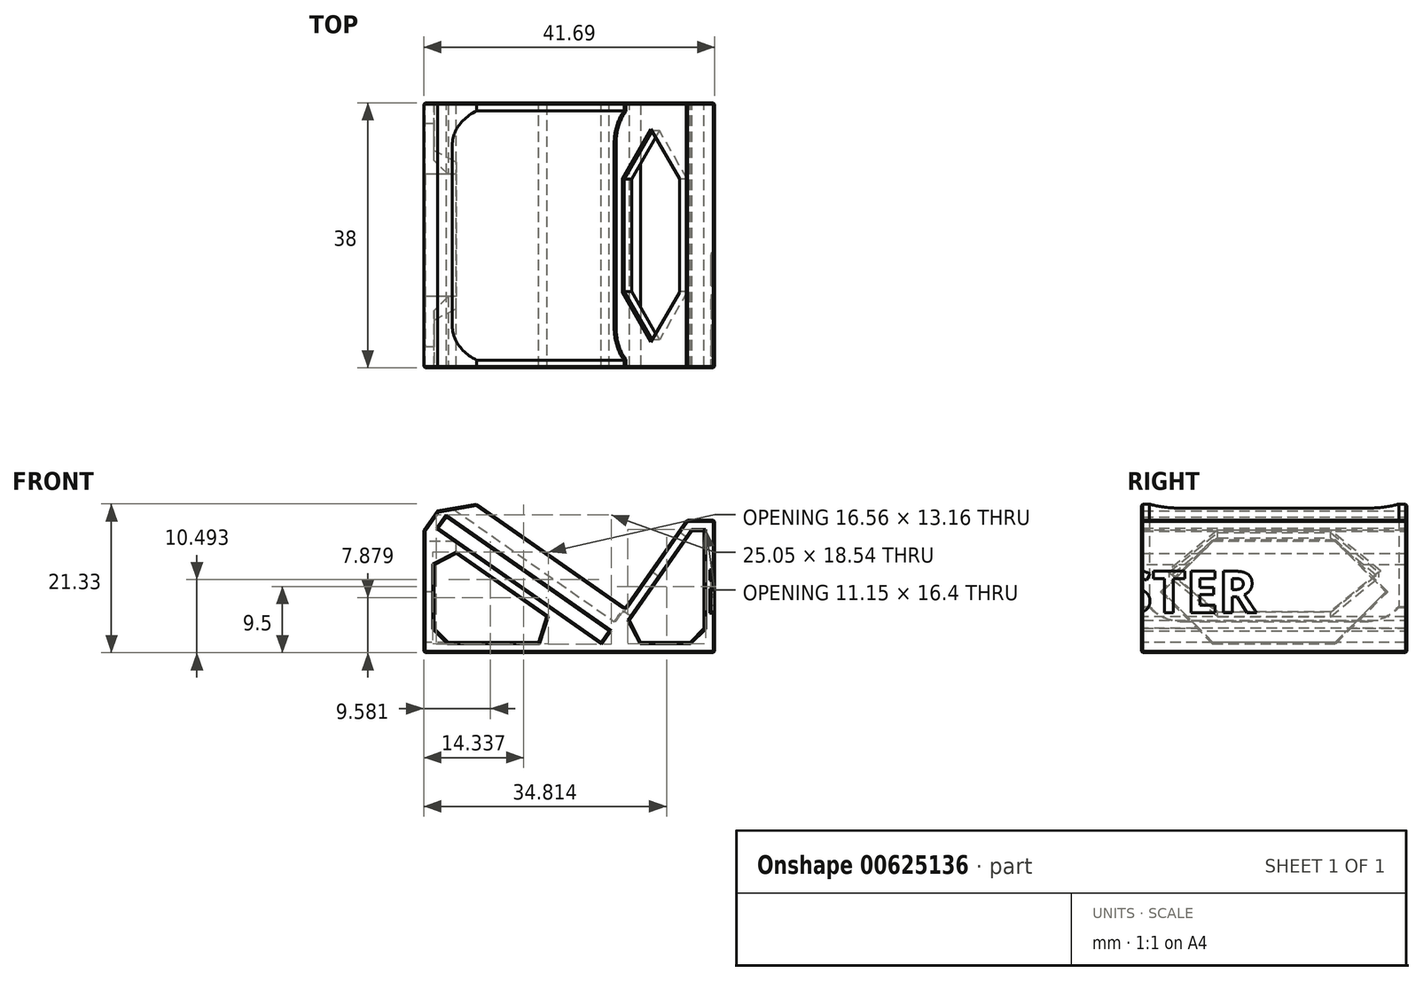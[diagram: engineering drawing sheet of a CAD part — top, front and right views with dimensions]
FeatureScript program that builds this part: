
annotation { "Feature Type Name" : "Feature", "Feature Type Description" : "" }
export const myFeature = defineFeature(function(context is Context, id is Id, definition is map)
    precondition{}
    {
        {
            var Q0;
            Q0=qCreatedBy(makeId("Front.planeOp"),FACE);
            var sketch = newSketch(context, id + "F0", { "sketchPlane" : qUnion([Q0])});
            skLineSegment(sketch, "E0", {"start": v(0, 0) * mm, "end": v(0, 19) * mm});
            skLineSegment(sketch, "E1", {"start": v(-4, 19) * mm, "end": v(-14.25, 4.37) * mm});
            skLineSegment(sketch, "E2", {"start": v(-14.25, 4.37) * mm, "end": v(-38.82, 21.57) * mm});
            skLineSegment(sketch, "E3", {"start": v(-18.87, 1.5) * mm, "end": v(-40.19, 16.43) * mm});
            skPoint(sketch, "E4", {"position": v(0, 0) * mm});
            skLineSegment(sketch, "E5", {"start": v(-38.45, 19.49) * mm, "end": v(-15.1, 3.14) * mm});
            skLineSegment(sketch, "E6", {"start": v(-15.1, 3.14) * mm, "end": v(-16.25, 1.5) * mm});
            skLineSegment(sketch, "E7", {"start": v(0, 19) * mm, "end": v(-4, 19) * mm});
            skLineSegment(sketch, "E8", {"start": v(-14.42, 1.5) * mm, "end": v(-3.22, 17.5) * mm});
            skLineSegment(sketch, "E9", {"start": v(-3.22, 17.5) * mm, "end": v(-1.5, 17.5) * mm});
            skLineSegment(sketch, "E10", {"start": v(-1.5, 17.5) * mm, "end": v(-1.5, 1.5) * mm});
            skLineSegment(sketch, "E11", {"start": v(-1.5, 1.5) * mm, "end": v(-14.42, 1.5) * mm});
            skLineSegment(sketch, "E12", {"start": v(-16.25, 1.5) * mm, "end": v(-39.6, 17.85) * mm});
            skLineSegment(sketch, "E13", {"start": v(-38.45, 19.49) * mm, "end": v(-39.6, 17.85) * mm});
            skLineSegment(sketch, "E14", {"start": v(-38.82, 21.57) * mm, "end": v(-41.69, 17.48) * mm});
            skLineSegment(sketch, "E15", {"start": v(-41.69, 17.48) * mm, "end": v(-41.69, 0) * mm});
            skLineSegment(sketch, "E16", {"start": v(-41.69, 0) * mm, "end": v(0, 0) * mm});
            skLineSegment(sketch, "E17.0", {"start": v(-40.19, 1.5) * mm, "end": v(-18.87, 1.5) * mm});
            skLineSegment(sketch, "E17.1", {"start": v(-40.19, 16.43) * mm, "end": v(-40.19, 1.5) * mm});
            skSolve(sketch);
        }
        {
            var Q0;
            {var subQ3=sQuery(id+"F0.wireOp",EDGE,"E2");Q0=makeQuery(id+"F0.imprint","IMPRINT",FACE,{"disambiguationData":[TD([[makeQuery(id+"F0.imprint","IMPRINT",EDGE,{"derivedFrom":subQ3}),1.0]])]});}
            extrude(context, id + "F1", {"entities" : qUnion([Q0]), "endBound" : BoundingType.SYMMETRIC, "depth" : 38 * mm, "offsetDistance" : 25 * mm});
        }
        {
            var Q0;
            Q0=makeQuery(id+"F1.opExtrude","SWEPT_FACE",FACE,{"disambiguationData":[OSD([sQuery(id+"F0.wireOp",EDGE,"E0")])]});
            var sketch = newSketch(context, id + "F2", { "sketchPlane" : qUnion([Q0])});
            skText(sketch, "E18", { "text": "AIRSTER", "fontName": "OpenSans-Bold.ttf"});
            skPoint(sketch, "E19", {"position": v(-17, 9.5) * mm});
            skPoint(sketch, "E20", {"position": v(-19, 9.5) * mm});
            skPoint(sketch, "E21", {"position": v(0, 19) * mm});
            const initialGuessF2  = {"E18": [-0.036, 0.00576, 1, 0, 0.00598]};
            skSetInitialGuess(sketch, initialGuessF2);
            skSolve(sketch);
        }
        {
            var Q0;
            Q0=qSketchRegion(id+"F2",true);
            extrude(context, id + "F3", {"entities" : qUnion([Q0]), "operationType" : NewBodyOperationType.REMOVE, "oppositeDirection" : true, "depth" : 0.5 * mm});
        }
        {
            var Q0;
            Q0=makeQuery(id+"F1.opExtrude","SWEPT_EDGE",EDGE,{"disambiguationData":[OSD([sQuery(id+"F0.wireOp",EDGE,"E8"),sQuery(id+"F0.wireOp",EDGE,"E11")])]});
            var Q1;
            Q1=makeQuery(id+"F1.opExtrude","SWEPT_EDGE",EDGE,{"disambiguationData":[OSD([sQuery(id+"F0.wireOp",EDGE,"E10"),sQuery(id+"F0.wireOp",EDGE,"E11")])]});
            var Q2;
            Q2=makeQuery(id+"F1.opExtrude","SWEPT_EDGE",EDGE,{"disambiguationData":[OSD([sQuery(id+"F0.wireOp",EDGE,"E17.0"),sQuery(id+"F0.wireOp",EDGE,"E17.1")])]});
            var Q3;
            Q3=makeQuery(id+"F1.opExtrude","SWEPT_EDGE",EDGE,{"disambiguationData":[OSD([sQuery(id+"F0.wireOp",EDGE,"E3"),sQuery(id+"F0.wireOp",EDGE,"E17.1")])]});
            chamfer(context, id + "F4", {"entities" : qUnion([Q0, Q1, Q2, Q3]), "width" : 2 * mm, "tangentPropagation" : true});
        }
        {
            var Q0;
            Q0=makeQuery(id+"F1.opExtrude","SWEPT_FACE",FACE,{"disambiguationData":[OSD([sQuery(id+"F0.wireOp",EDGE,"E1")])]});
            var sketch = newSketch(context, id + "F5", { "sketchPlane" : qUnion([Q0])});
            skArc(sketch, "E22", {"start": v(-19, 1.4) * mm, "mid": v(-17.24, -2.84) * mm, "end": v(-13, -4.6) * mm});
            skArc(sketch, "E23.MirrorCS", {"start": v(19, 1.4) * mm, "mid": v(17.24, -2.84) * mm, "end": v(13, -4.6) * mm});
            skLineSegment(sketch, "E24", {"start": v(-19, -2.1) * mm, "end": v(-17.87, -2.1) * mm});
            skLineSegment(sketch, "E25.MirrorCS", {"start": v(19, -2.1) * mm, "end": v(17.87, -2.1) * mm});
            skLineSegment(sketch, "E26", {"start": v(0, 11.27) * mm, "end": v(-15, 11.27) * mm});
            skLineSegment(sketch, "E27", {"start": v(-15, 11.27) * mm, "end": v(-15, -2.6) * mm});
            skLineSegment(sketch, "E28", {"start": v(-15, -2.6) * mm, "end": v(0, -2.6) * mm});
            skLineSegment(sketch, "E29.MirrorCS", {"start": v(0, 11.27) * mm, "end": v(15, 11.27) * mm});
            skLineSegment(sketch, "E30.MirrorCS", {"start": v(15, 11.27) * mm, "end": v(15, -2.6) * mm});
            skLineSegment(sketch, "E31.MirrorCS", {"start": v(15, -2.6) * mm, "end": v(0, -2.6) * mm});
            skPoint(sketch, "E32", {"position": v(-15, 4.34) * mm});
            skLineSegment(sketch, "E33", {"start": v(-15, 4.34) * mm, "end": v(-8.07, 11.27) * mm});
            skLineSegment(sketch, "E34", {"start": v(-15, 4.34) * mm, "end": v(-8.07, -2.6) * mm});
            skLineSegment(sketch, "E35.MirrorCS", {"start": v(15, 4.34) * mm, "end": v(8.07, 11.27) * mm});
            skLineSegment(sketch, "E36.MirrorCS", {"start": v(15, 4.34) * mm, "end": v(8.07, -2.6) * mm});
            skSolve(sketch);
        }
        {
            var Q0;
            {var subQ4=sQuery(id+"F5.wireOp",EDGE,"E24");Q0=makeQuery(id+"F5.imprint","IMPRINT",FACE,{"disambiguationData":[TD([[makeQuery(id+"F5.imprint","IMPRINT",EDGE,{"derivedFrom":subQ4}),-1.0]])]});}
            var Q1;
            {var subQ4=sQuery(id+"F5.wireOp",EDGE,"E25.MirrorCS");Q1=makeQuery(id+"F5.imprint","IMPRINT",FACE,{"disambiguationData":[TD([[makeQuery(id+"F5.imprint","IMPRINT",EDGE,{"derivedFrom":subQ4}),1.0]])]});}
            var Q2;
            Q2=makeQuery(id+"F1.opExtrude","SWEPT_FACE",FACE,{"disambiguationData":[OSD([sQuery(id+"F0.wireOp",EDGE,"E14")])]});
            extrude(context, id + "F6", {"entities" : qUnion([Q0, Q1]), "operationType" : NewBodyOperationType.ADD, "endBound" : BoundingType.UP_TO_SURFACE, "depth" : 25 * mm, "endBoundEntityFace" : qUnion([Q2]), "offsetDistance" : 25 * mm});
        }
        {
            var Q0;
            Q0=makeQuery(id+"F6.opExtrude","CAP_EDGE",EDGE,{"disambiguationData":[OSD([sQuery(id+"F5.wireOp",EDGE,"E24")])],"isStart":false});
            var Q1;
            Q1=makeQuery(id+"F6.opExtrude","CAP_EDGE",EDGE,{"disambiguationData":[OSD([sQuery(id+"F5.wireOp",EDGE,"E25.MirrorCS")])],"isStart":false});
            chamfer(context, id + "F7", {"entities" : qUnion([Q0, Q1]), "width" : 4 * mm, "tangentPropagation" : true});
        }
        {
            var Q0;
            {var subQ7=sQuery(id+"F5.wireOp",EDGE,"E33");Q0=makeQuery(id+"F5.imprint","IMPRINT",FACE,{"disambiguationData":[TD([[makeQuery(id+"F5.imprint","IMPRINT",EDGE,{"derivedFrom":subQ7}),-1.0]])]});}
            var Q1;
            Q1=makeQuery(id+"F1.opExtrude","SWEPT_FACE",FACE,{"disambiguationData":[OSD([sQuery(id+"F0.wireOp",EDGE,"E8")])]});
            extrude(context, id + "F8", {"entities" : qUnion([Q0]), "operationType" : NewBodyOperationType.REMOVE, "endBound" : BoundingType.UP_TO_SURFACE, "oppositeDirection" : true, "depth" : 25 * mm, "endBoundEntityFace" : qUnion([Q1]), "offsetDistance" : 25 * mm});
        }
        {
            var Q0;
            Q0=makeQuery(id+"F1.opExtrude","SWEPT_FACE",FACE,{"disambiguationData":[OSD([sQuery(id+"F0.wireOp",EDGE,"E15")])]});
            var sketch = newSketch(context, id + "F9", { "sketchPlane" : qUnion([Q0])});
            skLineSegment(sketch, "E37", {"start": v(0, 15.98) * mm, "end": v(-16, 15.98) * mm});
            skLineSegment(sketch, "E38", {"start": v(-16, 15.98) * mm, "end": v(-16, 1.5) * mm});
            skLineSegment(sketch, "E39", {"start": v(-16, 1.5) * mm, "end": v(0, 1.5) * mm});
            skPoint(sketch, "E40", {"position": v(-16, 8.74) * mm});
            skLineSegment(sketch, "E41", {"start": v(-16, 8.74) * mm, "end": v(-8.76, 15.98) * mm});
            skLineSegment(sketch, "E42", {"start": v(-16, 8.74) * mm, "end": v(-8.76, 1.5) * mm});
            skLineSegment(sketch, "E43.MirrorCS", {"start": v(0, 15.98) * mm, "end": v(16, 15.98) * mm});
            skLineSegment(sketch, "E44.MirrorCS", {"start": v(16, 8.74) * mm, "end": v(8.76, 15.98) * mm});
            skLineSegment(sketch, "E45.MirrorCS", {"start": v(16, 8.74) * mm, "end": v(8.76, 1.5) * mm});
            skLineSegment(sketch, "E46.MirrorCS", {"start": v(16, 1.5) * mm, "end": v(0, 1.5) * mm});
            skLineSegment(sketch, "E47.MirrorCS", {"start": v(16, 15.98) * mm, "end": v(16, 1.5) * mm});
            skSolve(sketch);
        }
        {
            var Q0;
            {var subQ1=sQuery(id+"F9.wireOp",EDGE,"E41");Q0=makeQuery(id+"F9.imprint","IMPRINT",FACE,{"disambiguationData":[TD([[makeQuery(id+"F9.imprint","IMPRINT",EDGE,{"derivedFrom":subQ1}),-1.0]])]});}
            var Q1;
            {var subQ0=sQuery(id+"F0.wireOp",EDGE,"E3");var subQ1=sQuery(id+"F0.wireOp",EDGE,"E17.1");Q1=makeQuery(id+"F4.opChamfer","BLEND_VERTEX",VERTEX,{"blendedFrom":[makeQuery(id+"F1.opExtrude","SWEPT_EDGE",EDGE,{"disambiguationData":[OSD([subQ0,subQ1])]}),makeQuery(id+"F1.opExtrude","CAP_FACE",FACE,{"disambiguationData":[OSD([sQuery(id+"F0.wireOp",EDGE,"E0"),sQuery(id+"F0.wireOp",EDGE,"E1"),sQuery(id+"F0.wireOp",EDGE,"E2"),subQ0,sQuery(id+"F0.wireOp",EDGE,"E5"),sQuery(id+"F0.wireOp",EDGE,"E6"),sQuery(id+"F0.wireOp",EDGE,"E7"),sQuery(id+"F0.wireOp",EDGE,"E8"),sQuery(id+"F0.wireOp",EDGE,"E9"),sQuery(id+"F0.wireOp",EDGE,"E10"),sQuery(id+"F0.wireOp",EDGE,"E11"),sQuery(id+"F0.wireOp",EDGE,"E12"),sQuery(id+"F0.wireOp",EDGE,"E13"),sQuery(id+"F0.wireOp",EDGE,"E14"),sQuery(id+"F0.wireOp",EDGE,"E15"),sQuery(id+"F0.wireOp",EDGE,"E16"),sQuery(id+"F0.wireOp",EDGE,"E17.0"),subQ1])],"isStart":true}),makeQuery(id+"F1.opExtrude","SWEPT_FACE",FACE,{"disambiguationData":[OSD([subQ0])]})],"blendedInto":[makeQuery(id+"F1.opExtrude","CAP_FACE",FACE,{"disambiguationData":[OSD([sQuery(id+"F0.wireOp",EDGE,"E0"),sQuery(id+"F0.wireOp",EDGE,"E1"),sQuery(id+"F0.wireOp",EDGE,"E2"),subQ0,sQuery(id+"F0.wireOp",EDGE,"E5"),sQuery(id+"F0.wireOp",EDGE,"E6"),sQuery(id+"F0.wireOp",EDGE,"E7"),sQuery(id+"F0.wireOp",EDGE,"E8"),sQuery(id+"F0.wireOp",EDGE,"E9"),sQuery(id+"F0.wireOp",EDGE,"E10"),sQuery(id+"F0.wireOp",EDGE,"E11"),sQuery(id+"F0.wireOp",EDGE,"E12"),sQuery(id+"F0.wireOp",EDGE,"E13"),sQuery(id+"F0.wireOp",EDGE,"E14"),sQuery(id+"F0.wireOp",EDGE,"E15"),sQuery(id+"F0.wireOp",EDGE,"E16"),sQuery(id+"F0.wireOp",EDGE,"E17.0"),subQ1])],"isStart":true}),makeQuery(id+"F1.opExtrude","SWEPT_FACE",FACE,{"disambiguationData":[OSD([subQ0])]})]});}
            extrude(context, id + "F10", {"entities" : qUnion([Q0]), "operationType" : NewBodyOperationType.REMOVE, "endBound" : BoundingType.UP_TO_VERTEX, "oppositeDirection" : true, "depth" : 25 * mm, "endBoundEntityVertex" : qUnion([Q1]), "offsetDistance" : 25 * mm});
        }
        {
            var Q0;
            Q0=makeQuery(id+"F1.opExtrude","SWEPT_EDGE",EDGE,{"disambiguationData":[OSD([sQuery(id+"F0.wireOp",EDGE,"E3"),sQuery(id+"F0.wireOp",EDGE,"E17.0")])]});
            chamfer(context, id + "F11", {"entities" : qUnion([Q0]), "width" : 2 * mm, "tangentPropagation" : true});
        }
        {
            var Q0;
            {var subQ0=sQuery(id+"F0.wireOp",EDGE,"E1");var subQ1=makeQuery(id+"F1.opExtrude","CAP_EDGE",EDGE,{"disambiguationData":[OSD([subQ0])],"isStart":false});var subQ2=sQuery(id+"F0.wireOp",EDGE,"E2");Q0=makeQuery(id+"F6.boolean.opBoolean","MERGE",FACE,{"derivedFrom":[makeQuery(id+"F1.opExtrude","CAP_FACE",FACE,{"disambiguationData":[OSD([sQuery(id+"F0.wireOp",EDGE,"E0"),subQ0,subQ2,sQuery(id+"F0.wireOp",EDGE,"E3"),sQuery(id+"F0.wireOp",EDGE,"E5"),sQuery(id+"F0.wireOp",EDGE,"E6"),sQuery(id+"F0.wireOp",EDGE,"E7"),sQuery(id+"F0.wireOp",EDGE,"E8"),sQuery(id+"F0.wireOp",EDGE,"E9"),sQuery(id+"F0.wireOp",EDGE,"E10"),sQuery(id+"F0.wireOp",EDGE,"E11"),sQuery(id+"F0.wireOp",EDGE,"E12"),sQuery(id+"F0.wireOp",EDGE,"E13"),sQuery(id+"F0.wireOp",EDGE,"E14"),sQuery(id+"F0.wireOp",EDGE,"E15"),sQuery(id+"F0.wireOp",EDGE,"E16"),sQuery(id+"F0.wireOp",EDGE,"E17.0"),sQuery(id+"F0.wireOp",EDGE,"E17.1")])],"isStart":false}),makeQuery(id+"F6.opExtrude","SWEPT_FACE",FACE,{"disambiguationData":[OSD([subQ0]),TDD([makeQuery(id+"F5.imprint","IMPRINT",EDGE,{"disambiguationData":[TD([[makeQuery(id+"F5.imprint","INTERSECT",VERTEX,{"derivedFrom":[subQ1,sQuery(id+"F5.wireOp",EDGE,"E25.MirrorCS")]}),-1.0]])],"derivedFrom":subQ1})])]})]});}
            var Q1;
            Q1=makeQuery(id+"F1.opExtrude","SWEPT_FACE",FACE,{"disambiguationData":[OSD([sQuery(id+"F0.wireOp",EDGE,"E15")])]});
            var Q2;
            Q2=makeQuery(id+"F1.opExtrude","SWEPT_FACE",FACE,{"disambiguationData":[OSD([sQuery(id+"F0.wireOp",EDGE,"E1")])]});
            var Q3;
            {var subQ0=sQuery(id+"F0.wireOp",EDGE,"E1");var subQ1=makeQuery(id+"F1.opExtrude","CAP_EDGE",EDGE,{"disambiguationData":[OSD([subQ0])],"isStart":true});var subQ2=sQuery(id+"F0.wireOp",EDGE,"E2");Q3=makeQuery(id+"F6.boolean.opBoolean","MERGE",FACE,{"derivedFrom":[makeQuery(id+"F1.opExtrude","CAP_FACE",FACE,{"disambiguationData":[OSD([sQuery(id+"F0.wireOp",EDGE,"E0"),subQ0,subQ2,sQuery(id+"F0.wireOp",EDGE,"E3"),sQuery(id+"F0.wireOp",EDGE,"E5"),sQuery(id+"F0.wireOp",EDGE,"E6"),sQuery(id+"F0.wireOp",EDGE,"E7"),sQuery(id+"F0.wireOp",EDGE,"E8"),sQuery(id+"F0.wireOp",EDGE,"E9"),sQuery(id+"F0.wireOp",EDGE,"E10"),sQuery(id+"F0.wireOp",EDGE,"E11"),sQuery(id+"F0.wireOp",EDGE,"E12"),sQuery(id+"F0.wireOp",EDGE,"E13"),sQuery(id+"F0.wireOp",EDGE,"E14"),sQuery(id+"F0.wireOp",EDGE,"E15"),sQuery(id+"F0.wireOp",EDGE,"E16"),sQuery(id+"F0.wireOp",EDGE,"E17.0"),sQuery(id+"F0.wireOp",EDGE,"E17.1")])],"isStart":true}),makeQuery(id+"F6.opExtrude","SWEPT_FACE",FACE,{"disambiguationData":[OSD([subQ0]),TDD([makeQuery(id+"F5.imprint","IMPRINT",EDGE,{"disambiguationData":[TD([[makeQuery(id+"F5.imprint","INTERSECT",VERTEX,{"derivedFrom":[subQ1,sQuery(id+"F5.wireOp",EDGE,"E24")]}),-1.0]])],"derivedFrom":subQ1})])]})]});}
            var Q4;
            Q4=makeQuery(id+"F1.opExtrude","SWEPT_EDGE",EDGE,{"disambiguationData":[OSD([sQuery(id+"F0.wireOp",EDGE,"E0"),sQuery(id+"F0.wireOp",EDGE,"E7")])]});
            var Q5;
            Q5=makeQuery(id+"F1.opExtrude","SWEPT_EDGE",EDGE,{"disambiguationData":[OSD([sQuery(id+"F0.wireOp",EDGE,"E0"),sQuery(id+"F0.wireOp",EDGE,"E16")])]});
            chamfer(context, id + "F12", {"entities" : qUnion([Q0, Q1, Q2, Q3, Q4, Q5]), "width" : 0.2 * mm, "tangentPropagation" : true});
        }
    });
